# Revit family: ASSA_ABLOY_MPD_RP300
name_source: partatom
category: Doors
units: mm (PartAtom-declared; Revit-internal decimal feet)

## family parameters
Always vertical = Yes
Cut with Voids When Loaded = No
Host = Wall
Room Calculation Point = No
Shared = No

## types (1)
- Type 1
    AluSideFrames = Yes
    AlumuniumMaterial = Aluminum
    Analytic Construction = <None>
    BracketMaterial = Steel Galvanized
    ClearanceZoneMaterial = ASSA ABLOY Clearance Zone
    Description = Machine Protection Door
    Manufacturer = ASSA ABLOY
    Model = RP300
    NoiseReduction = < 70 dB A
    NotChainDriveRight = Yes
    Operating speed = Max. 1,0 m/s / 1,0 m/s
    PowerSupply = 3L(N)PE/230/380/400/415V; 50Hz, transformer for 440/480/500V necessary
    RuleTopDoorCurtain1.3mmWithVisionPanel = No
    RuleTopDoorCurtain1.3mmWithoutVisionPanel = No
    StainlessSteelMaterial = Steel Galvanized
    StainlessSteelSideFrames = No
    Temperature working range = +10 °C to +45 °C
    TopDoorCurtain1.3mmWithVisionPanel = No
    TopDoorCurtain1.3mmWithoutVisionPanel = No
    URL = https://www.assaabloyentrance.com
    Width = 250 mm  [stored 0.82021 ft]
    Wind Resistance (EN 12424) = Class 1 (up to 11,0 m2)

note: [stored X ft] marks values corroborated as IEEE doubles in the binary element streams (Revit-internal decimal feet)

## geometry (parser evidence)
native form markers: Sweep x34
no freeform markers — native parametric forms only
